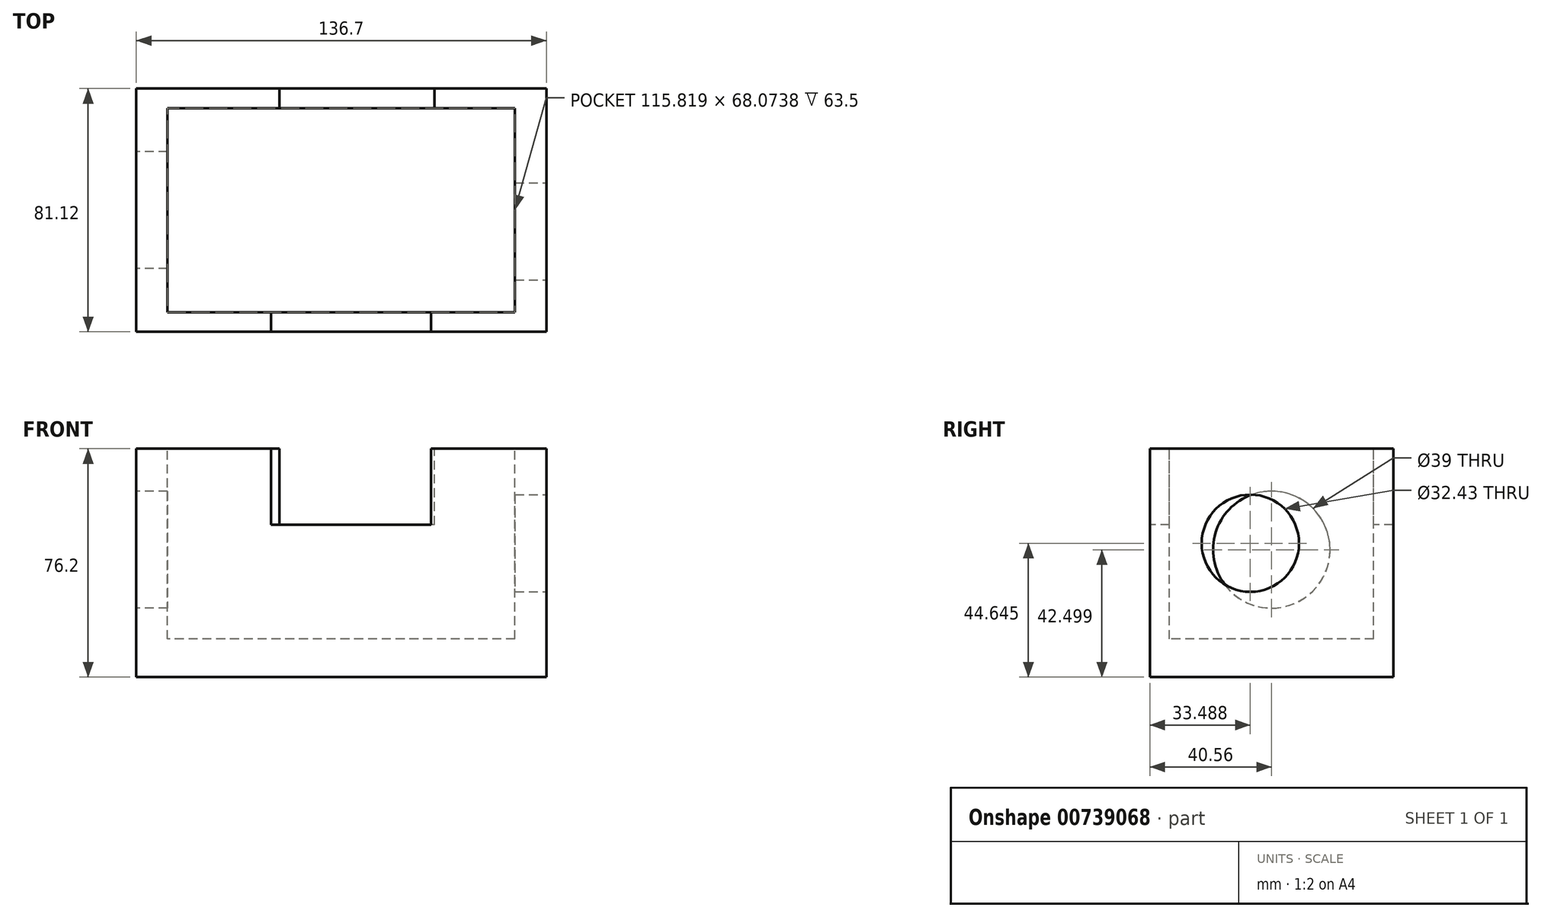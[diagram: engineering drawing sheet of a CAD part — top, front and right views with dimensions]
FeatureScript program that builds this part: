
annotation { "Feature Type Name" : "Feature", "Feature Type Description" : "" }
export const myFeature = defineFeature(function(context is Context, id is Id, definition is map)
    precondition{}
    {
        {
            var Q0;
            Q0=qCreatedBy(makeId("Top.planeOp"),FACE);
            var sketch = newSketch(context, id + "F0", { "sketchPlane" : qUnion([Q0])});
            skLineSegment(sketch, "E0.bottom", {"start": v(68.35, 40.56) * mm, "end": v(-68.35, 40.56) * mm});
            skLineSegment(sketch, "E0.top", {"start": v(68.35, -40.56) * mm, "end": v(-68.35, -40.56) * mm});
            skLineSegment(sketch, "E0.left", {"start": v(68.35, 40.56) * mm, "end": v(68.35, -40.56) * mm});
            skLineSegment(sketch, "E0.right", {"start": v(-68.35, 40.56) * mm, "end": v(-68.35, -40.56) * mm});
            skPoint(sketch, "E0.middle", {"position": v(0, 0) * mm});
            skSolve(sketch);
        }
        {
            var Q0;
            Q0=makeQuery(id+"F0.imprint","IMPRINT",FACE,{"disambiguationData":[TD([[makeQuery(id+"F0.imprint","IMPRINT",EDGE,{"derivedFrom":sQuery(id+"F0.wireOp",EDGE,"E0.bottom")}),1.0]])]});
            extrude(context, id + "F1", {"entities" : qUnion([Q0]), "depth" : 76.2 * mm, "offsetDistance" : 25.4 * mm});
        }
        {
            var Q0;
            Q0=makeQuery(id+"F1.opExtrude","CAP_FACE",FACE,{"disambiguationData":[OSD([sQuery(id+"F0.wireOp",EDGE,"E0.bottom"),sQuery(id+"F0.wireOp",EDGE,"E0.top"),sQuery(id+"F0.wireOp",EDGE,"E0.left"),sQuery(id+"F0.wireOp",EDGE,"E0.right")])],"isStart":false});
            var sketch = newSketch(context, id + "F2", { "sketchPlane" : qUnion([Q0])});
            skLineSegment(sketch, "E1.bottom", {"start": v(57.9, 34.04) * mm, "end": v(-57.9, 34.04) * mm});
            skLineSegment(sketch, "E1.top", {"start": v(57.9, -34.04) * mm, "end": v(-57.9, -34.04) * mm});
            skLineSegment(sketch, "E1.left", {"start": v(57.9, 34.04) * mm, "end": v(57.9, -34.04) * mm});
            skLineSegment(sketch, "E1.right", {"start": v(-57.9, 34.04) * mm, "end": v(-57.9, -34.04) * mm});
            skPoint(sketch, "E1.middle", {"position": v(0, 0) * mm});
            skSolve(sketch);
        }
        {
            var Q0;
            Q0 = qSketchRegion(id + "F2", true);
            extrude(context, id + "F3", {"entities" : qUnion([Q0]), "operationType" : NewBodyOperationType.REMOVE, "oppositeDirection" : true, "depth" : 63.5 * mm, "offsetDistance" : 25.4 * mm});
        }
        {
            var Q0;
            Q0=makeQuery(id+"F1.opExtrude","CAP_FACE",FACE,{"disambiguationData":[OSD([sQuery(id+"F0.wireOp",EDGE,"E0.bottom"),sQuery(id+"F0.wireOp",EDGE,"E0.top"),sQuery(id+"F0.wireOp",EDGE,"E0.left"),sQuery(id+"F0.wireOp",EDGE,"E0.right")])],"isStart":false});
            var sketch = newSketch(context, id + "F4", { "sketchPlane" : qUnion([Q0])});
            skLineSegment(sketch, "E2", {"start": v(31.1, 40.56) * mm, "end": v(31.1, 34.04) * mm});
            skLineSegment(sketch, "E3", {"start": v(-20.64, 40.56) * mm, "end": v(-20.64, 34.04) * mm});
            skLineSegment(sketch, "E4", {"start": v(33.06, -34.04) * mm, "end": v(31.98, -40.56) * mm});
            skLineSegment(sketch, "E5", {"start": v(-14.57, -34.04) * mm, "end": v(-16.18, -40.56) * mm});
            skSolve(sketch);
        }
        {
            var Q0;
            Q0 = qSketchRegion(id + "F4", true);
            var Q1;
            {var subQ0=sQuery(id+"F4.wireOp",EDGE,"E2");Q1=makeQuery(id+"F4.imprint","IMPRINT",FACE,{"disambiguationData":[TD([[makeQuery(id+"F4.imprint","IMPRINT",EDGE,{"derivedFrom":subQ0}),-1.0]])]});}
            extrude(context, id + "F5", {"entities" : qUnion([Q0, Q1]), "operationType" : NewBodyOperationType.REMOVE, "oppositeDirection" : true, "depth" : 25.4 * mm, "offsetDistance" : 25.4 * mm});
        }
        {
            var Q0;
            Q0=makeQuery(id+"F1.opExtrude","CAP_FACE",FACE,{"disambiguationData":[OSD([sQuery(id+"F0.wireOp",EDGE,"E0.bottom"),sQuery(id+"F0.wireOp",EDGE,"E0.top"),sQuery(id+"F0.wireOp",EDGE,"E0.left"),sQuery(id+"F0.wireOp",EDGE,"E0.right")])],"isStart":false});
            var sketch = newSketch(context, id + "F6", { "sketchPlane" : qUnion([Q0])});
            skLineSegment(sketch, "E6", {"start": v(29.94, -34.04) * mm, "end": v(29.94, -40.56) * mm});
            skLineSegment(sketch, "E7", {"start": v(-23.38, -34.04) * mm, "end": v(-23.38, -40.56) * mm});
            skSolve(sketch);
        }
        {
            var Q0;
            Q0 = qSketchRegion(id + "F6", true);
            var Q1;
            {var subQ0=sQuery(id+"F6.wireOp",EDGE,"E6");Q1=makeQuery(id+"F6.imprint","IMPRINT",FACE,{"disambiguationData":[TD([[makeQuery(id+"F6.imprint","IMPRINT",EDGE,{"derivedFrom":subQ0}),-1.0]])]});}
            extrude(context, id + "F7", {"entities" : qUnion([Q0, Q1]), "operationType" : NewBodyOperationType.REMOVE, "oppositeDirection" : true, "depth" : 25.4 * mm, "offsetDistance" : 25.4 * mm});
        }
        {
            var Q0;
            Q0=makeQuery(id+"F1.opExtrude","SWEPT_FACE",FACE,{"disambiguationData":[OSD([sQuery(id+"F0.wireOp",EDGE,"E0.right")])]});
            var sketch = newSketch(context, id + "F8", { "sketchPlane" : qUnion([Q0])});
            skCircle(sketch, "E8", {"center": v(0, 42.5) * mm, "radius": 19.5 * mm});
            skSolve(sketch);
        }
        {
            var Q0;
            Q0 = qSketchRegion(id + "F8", true);
            var Q1;
            Q1=makeQuery(id+"F8.imprint","IMPRINT",FACE,{"disambiguationData":[TD([[makeQuery(id+"F8.imprint","IMPRINT",EDGE,{"derivedFrom":sQuery(id+"F8.wireOp",EDGE,"E8")}),1.0]])]});
            extrude(context, id + "F9", {"entities" : qUnion([Q0, Q1]), "operationType" : NewBodyOperationType.REMOVE, "oppositeDirection" : true, "depth" : 25.4 * mm, "offsetDistance" : 25.4 * mm});
        }
        {
            var Q0;
            Q0=makeQuery(id+"F1.opExtrude","SWEPT_FACE",FACE,{"disambiguationData":[OSD([sQuery(id+"F0.wireOp",EDGE,"E0.left")])]});
            var sketch = newSketch(context, id + "F10", { "sketchPlane" : qUnion([Q0])});
            skCircle(sketch, "E9", {"center": v(-7.07, 44.64) * mm, "radius": 16.22 * mm});
            skSolve(sketch);
        }
        {
            var Q0;
            Q0 = qSketchRegion(id + "F10", true);
            extrude(context, id + "F11", {"entities" : qUnion([Q0]), "operationType" : NewBodyOperationType.REMOVE, "oppositeDirection" : true, "depth" : 25.4 * mm, "offsetDistance" : 25.4 * mm});
        }
    });
